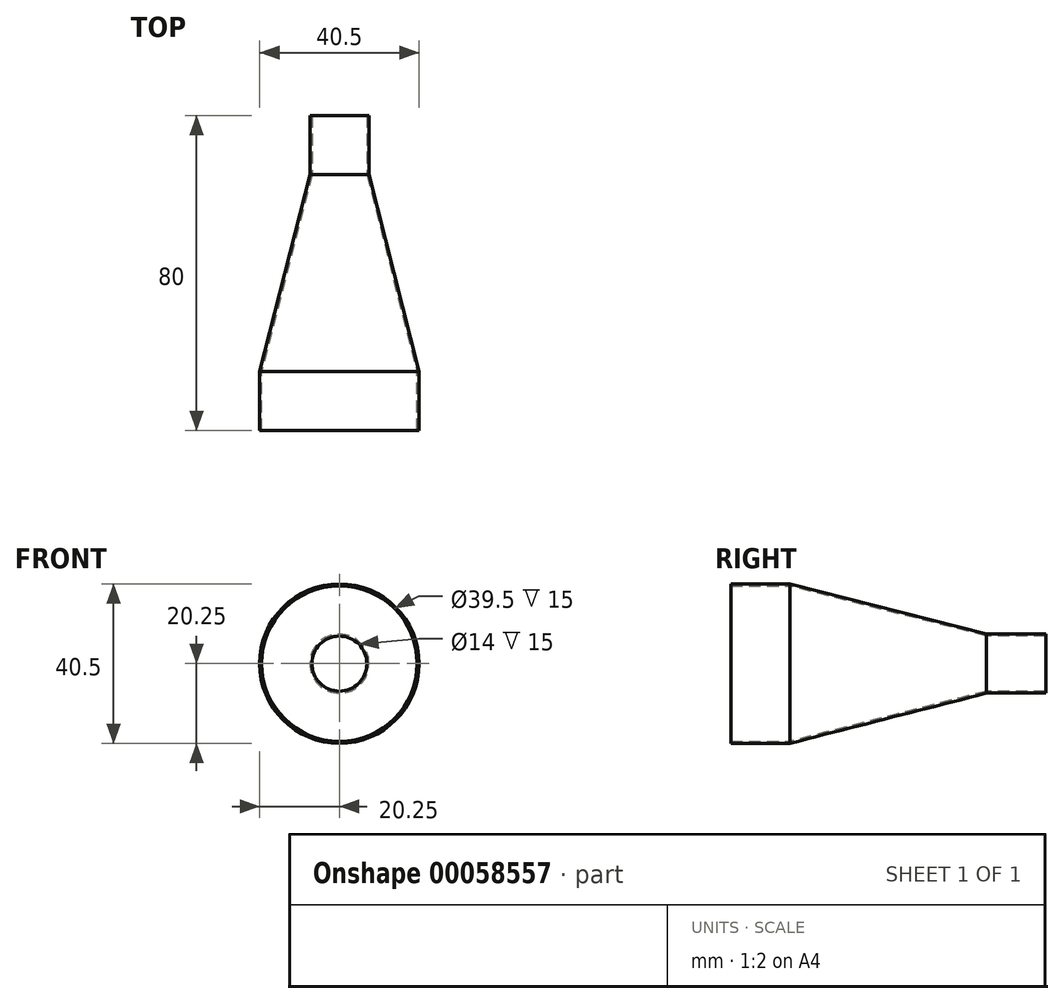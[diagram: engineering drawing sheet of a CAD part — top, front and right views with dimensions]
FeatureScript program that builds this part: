
annotation { "Feature Type Name" : "Feature", "Feature Type Description" : "" }
export const myFeature = defineFeature(function(context is Context, id is Id, definition is map)
    precondition{}
    {
        {
            var Q0;
            Q0=qCreatedBy(makeId("Front.planeOp"),FACE);
            var sketch = newSketch(context, id + "F0", { "sketchPlane" : qUnion([Q0])});
            skCircle(sketch, "E0", {"center": v(0, 0) * mm, "radius": 20.25 * mm});
            skSolve(sketch);
        }
        {
            var Q0;
            Q0=qCreatedBy(makeId("Front.planeOp"),FACE);
            cPlane(context, id + "F1", {"entities" : qUnion([Q0]), "cplaneType" : CPlaneType.OFFSET, "offset" : 50 * mm, "oppositeDirection" : true, "width" : 150 * mm, "height" : 150 * mm});
        }
        {
            var Q0;
            Q0=qCreatedBy(id+"F1.planeOp",FACE);
            var sketch = newSketch(context, id + "F2", { "sketchPlane" : qUnion([Q0])});
            skCircle(sketch, "E1", {"center": v(0, 0) * mm, "radius": 7.5 * mm});
            skSolve(sketch);
        }
        {
            var Q0;
            Q0 = qSketchRegion(id + "F0", true);
            var Q1;
            Q1 = qSketchRegion(id + "F2", true);
            loft(context, id + "F3", {"sheetProfilesArray" : [{ "sheetProfileEntities" : qUnion([Q0]) }, { "sheetProfileEntities" : qUnion([Q1]) }]});
        }
        {
            var Q0;
            Q0=qCreatedBy(makeId("Front.planeOp"),FACE);
            var sketch = newSketch(context, id + "F4", { "sketchPlane" : qUnion([Q0])});
            skCircle(sketch, "E2", {"center": v(0, 0) * mm, "radius": 19.75 * mm});
            skSolve(sketch);
        }
        {
            var Q0;
            Q0=qCreatedBy(id+"F1.planeOp",FACE);
            var sketch = newSketch(context, id + "F5", { "sketchPlane" : qUnion([Q0])});
            skCircle(sketch, "E3", {"center": v(0, 0) * mm, "radius": 7 * mm});
            skSolve(sketch);
        }
        {
            var Q1;
            Q1 = qSketchRegion(id + "F4", true);
            var Q2;
            Q2 = qSketchRegion(id + "F5", true);
            loft(context, id + "F6", {"operationType" : NewBodyOperationType.REMOVE, "sheetProfilesArray" : [{ "sheetProfileEntities" : qUnion([Q1]) }, { "sheetProfileEntities" : qUnion([Q2]) }]});
        }
        {
            var Q0;
            Q0=makeQuery(id+"F3.opLoft","CAP_FACE",FACE,{"disambiguationData":[OSD([makeQuery(id+"F0.imprint","IMPRINT",FACE,{"disambiguationData":[TD([[makeQuery(id+"F0.imprint","IMPRINT",EDGE,{"derivedFrom":sQuery(id+"F0.wireOp",EDGE,"E0")}),1.0]])]})])],"isStart":true});
            extrude(context, id + "F7", {"entities" : qUnion([Q0]), "operationType" : NewBodyOperationType.ADD, "depth" : 15 * mm});
        }
        {
            var Q0;
            Q0=makeQuery(id+"F3.opLoft","CAP_FACE",FACE,{"disambiguationData":[OSD([makeQuery(id+"F2.imprint","IMPRINT",FACE,{"disambiguationData":[TD([[makeQuery(id+"F2.imprint","IMPRINT",EDGE,{"derivedFrom":sQuery(id+"F2.wireOp",EDGE,"E1")}),1.0]])]})])],"isStart":true});
            extrude(context, id + "F8", {"entities" : qUnion([Q0]), "operationType" : NewBodyOperationType.ADD, "depth" : 15 * mm});
        }
    });
